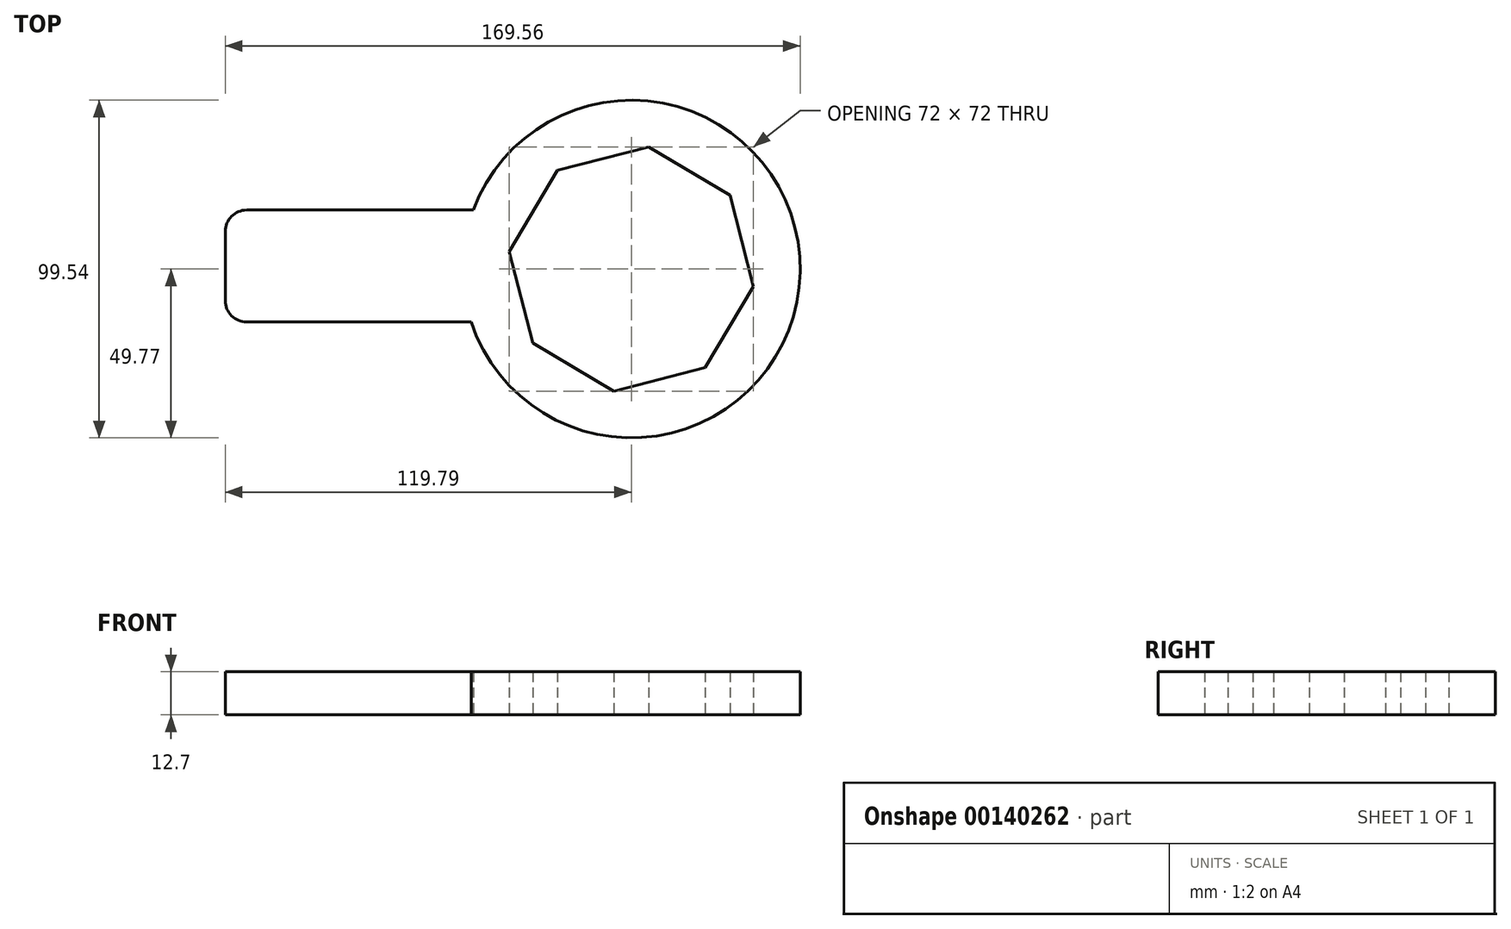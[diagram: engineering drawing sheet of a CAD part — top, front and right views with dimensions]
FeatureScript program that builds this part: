
annotation { "Feature Type Name" : "Feature", "Feature Type Description" : "" }
export const myFeature = defineFeature(function(context is Context, id is Id, definition is map)
    precondition{}
    {
        {
            var Q0;
            Q0=qCreatedBy(makeId("Top.planeOp"),FACE);
            var sketch = newSketch(context, id + "F0", { "sketchPlane" : qUnion([Q0])});
            skCircle(sketch, "E0.cCircle", {"center": v(0, 0) * mm, "radius": 33.6 * mm, "construction": true});
            skLineSegment(sketch, "E0.0", {"start": v(36, -5.16) * mm, "end": v(21.8, -29.1) * mm});
            skLineSegment(sketch, "E0.1", {"start": v(21.8, -29.1) * mm, "end": v(-5.16, -36) * mm});
            skLineSegment(sketch, "E0.2", {"start": v(-5.16, -36) * mm, "end": v(-29.1, -21.8) * mm});
            skLineSegment(sketch, "E0.3", {"start": v(-29.1, -21.8) * mm, "end": v(-36, 5.16) * mm});
            skLineSegment(sketch, "E0.4", {"start": v(-36, 5.16) * mm, "end": v(-21.8, 29.1) * mm});
            skLineSegment(sketch, "E0.5", {"start": v(-21.8, 29.1) * mm, "end": v(5.16, 36) * mm});
            skLineSegment(sketch, "E0.6", {"start": v(5.16, 36) * mm, "end": v(29.1, 21.8) * mm});
            skLineSegment(sketch, "E0.7", {"start": v(29.1, 21.8) * mm, "end": v(36, -5.16) * mm});
            skPoint(sketch, "E0.0.midPoint", {"position": v(28.9, -17.13) * mm});
            skArc(sketch, "E1", {"start": v(-47.24, -15.64) * mm, "mid": v(49.76, -0.91) * mm, "end": v(-46.64, 17.37) * mm});
            skLineSegment(sketch, "E2.bottom", {"start": v(-46.64, 17.37) * mm, "end": v(-113.44, 17.37) * mm});
            skLineSegment(sketch, "E2.top", {"start": v(-46.64, -15.64) * mm, "end": v(-113.44, -15.64) * mm});
            skLineSegment(sketch, "E2.right", {"start": v(-119.8, 11.02) * mm, "end": v(-119.8, -9.3) * mm});
            skPoint(sketch, "E3.visualSharp", {"position": v(-119.8, 17.37) * mm});
            skArc(sketch, "E3.filletArc", {"start": v(-113.44, 17.37) * mm, "mid": v(-117.93, 15.51) * mm, "end": v(-119.8, 11.02) * mm});
            skPoint(sketch, "E4.visualSharp", {"position": v(-119.8, -15.64) * mm});
            skArc(sketch, "E4.filletArc", {"start": v(-119.8, -9.3) * mm, "mid": v(-117.93, -13.78) * mm, "end": v(-113.44, -15.64) * mm});
            skSolve(sketch);
        }
        {
            var Q0;
            Q0 = qSketchRegion(id + "F0", true);
            extrude(context, id + "F1", {"entities" : qUnion([Q0]), "depth" : 12.7 * mm});
        }
    });
